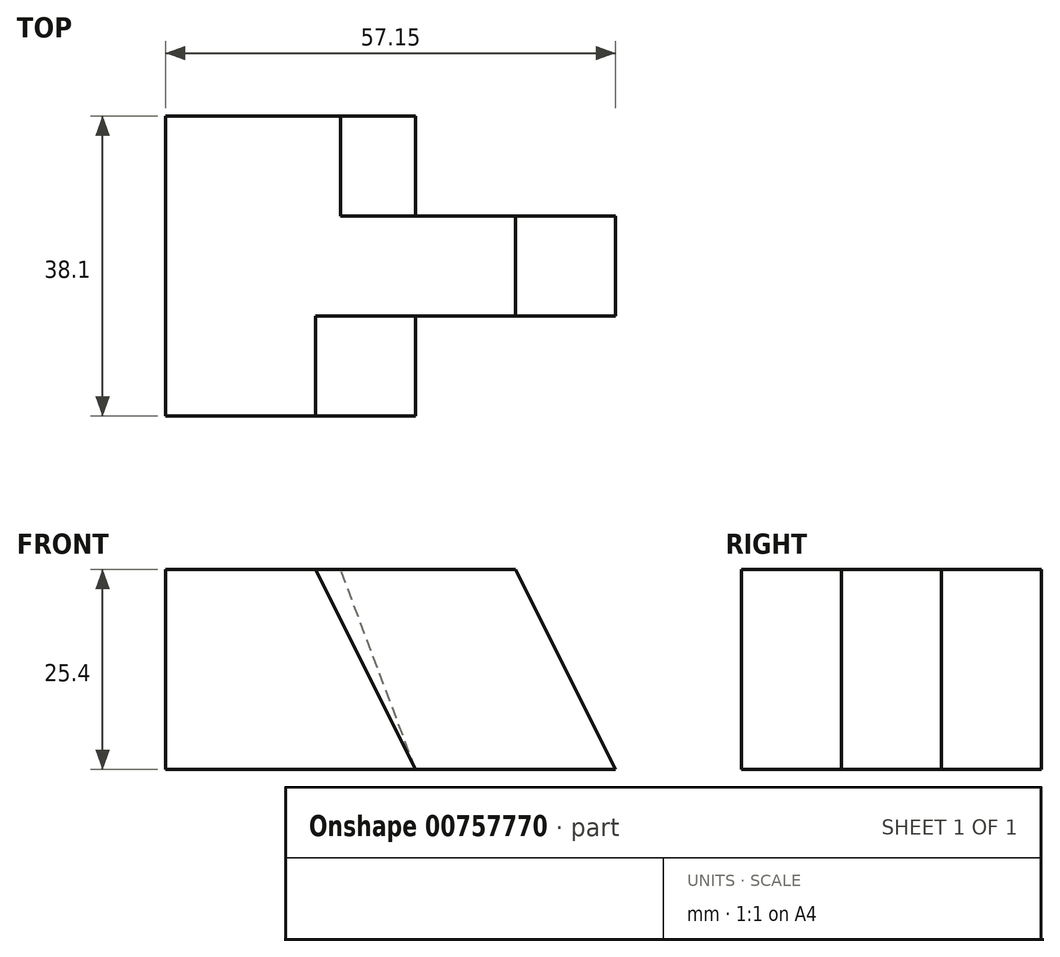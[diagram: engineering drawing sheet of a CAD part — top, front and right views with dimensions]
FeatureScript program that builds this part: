
annotation { "Feature Type Name" : "Feature", "Feature Type Description" : "" }
export const myFeature = defineFeature(function(context is Context, id is Id, definition is map)
    precondition{}
    {
        {
            var Q0;
            Q0=qCreatedBy(makeId("Right.planeOp"),FACE);
            var sketch = newSketch(context, id + "F0", { "sketchPlane" : qUnion([Q0])});
            skLineSegment(sketch, "E0", {"start": v(-16.78, 0) * mm, "end": v(21.32, 0) * mm});
            skLineSegment(sketch, "E1", {"start": v(21.32, 0) * mm, "end": v(21.32, 25.4) * mm});
            skLineSegment(sketch, "E2", {"start": v(21.32, 25.4) * mm, "end": v(-16.78, 25.4) * mm});
            skLineSegment(sketch, "E3", {"start": v(-16.78, 25.4) * mm, "end": v(-16.78, 0) * mm});
            skSolve(sketch);
        }
        {
            var Q0;
            Q0 = qSketchRegion(id + "F0", true);
            extrude(context, id + "F1", {"entities" : qUnion([Q0]), "depth" : 57.15 * mm, "offsetDistance" : 25.4 * mm});
        }
        {
            var Q0;
            Q0=makeQuery(id+"F1.opExtrude","SWEPT_FACE",FACE,{"disambiguationData":[OSD([sQuery(id+"F0.wireOp",EDGE,"E3")])]});
            var sketch = newSketch(context, id + "F2", { "sketchPlane" : qUnion([Q0])});
            skLineSegment(sketch, "E4", {"start": v(57.15, 0) * mm, "end": v(44.45, 25.4) * mm});
            skLineSegment(sketch, "E5", {"start": v(44.45, 25.4) * mm, "end": v(57.15, 25.4) * mm});
            skLineSegment(sketch, "E6", {"start": v(57.15, 25.4) * mm, "end": v(57.15, 0) * mm});
            skSolve(sketch);
        }
        {
            var Q0;
            Q0 = qSketchRegion(id + "F2", true);
            extrude(context, id + "F3", {"entities" : qUnion([Q0]), "operationType" : NewBodyOperationType.REMOVE, "endBound" : BoundingType.THROUGH_ALL, "oppositeDirection" : true, "depth" : 25.4 * mm, "offsetDistance" : 25.4 * mm});
        }
        {
            var Q0;
            {var subQ0=sQuery(id+"F2.wireOp",EDGE,"E4");Q0=makeQuery(id+"F2.imprint","IMPRINT",FACE,{"disambiguationData":[TD([[makeQuery(id+"F2.imprint","IMPRINT",EDGE,{"derivedFrom":subQ0}),1.0]])]});}
            var sketch = newSketch(context, id + "F4", { "sketchPlane" : qUnion([Q0])});
            skLineSegment(sketch, "E7", {"start": v(69.85, -25.56) * mm, "end": v(69.85, 2.84) * mm});
            skLineSegment(sketch, "E8", {"start": v(31.75, -25.56) * mm, "end": v(31.75, 2.84) * mm});
            skLineSegment(sketch, "E9", {"start": v(19.05, 25.43) * mm, "end": v(31.75, 0) * mm});
            skSolve(sketch);
        }
        {
            var Q0;
            Q0 = qSketchRegion(id + "F4", true);
            var Q1;
            {var subQ5=sQuery(id+"F2.wireOp",EDGE,"E4");var subQ8=makeQuery(id+"F2.imprint","IMPRINT",EDGE,{"derivedFrom":subQ5});Q1=makeQuery(id+"F4.imprint","IMPRINT",FACE,{"disambiguationData":[TD([[makeQuery(id+"F4.imprint","IMPRINT",EDGE,{"derivedFrom":subQ8}),1.0]])]});}
            extrude(context, id + "F5", {"entities" : qUnion([Q0, Q1]), "operationType" : NewBodyOperationType.REMOVE, "oppositeDirection" : true, "depth" : 12.7 * mm, "offsetDistance" : 25.4 * mm});
        }
        {
            var Q0;
            Q0=makeQuery(id+"F1.opExtrude","SWEPT_FACE",FACE,{"disambiguationData":[OSD([sQuery(id+"F0.wireOp",EDGE,"E1")])]});
            var sketch = newSketch(context, id + "F6", { "sketchPlane" : qUnion([Q0])});
            skLineSegment(sketch, "E10", {"start": v(-31.75, 0) * mm, "end": v(-22.23, 25.4) * mm});
            skSolve(sketch);
        }
        {
            var Q0;
            {var subQ0=sQuery(id+"F6.wireOp",EDGE,"E10");Q0=makeQuery(id+"F6.imprint","IMPRINT",FACE,{"disambiguationData":[TD([[makeQuery(id+"F6.imprint","IMPRINT",EDGE,{"derivedFrom":subQ0}),1.0]])]});}
            extrude(context, id + "F7", {"entities" : qUnion([Q0]), "operationType" : NewBodyOperationType.REMOVE, "oppositeDirection" : true, "depth" : 12.7 * mm, "offsetDistance" : 25.4 * mm});
        }
    });
